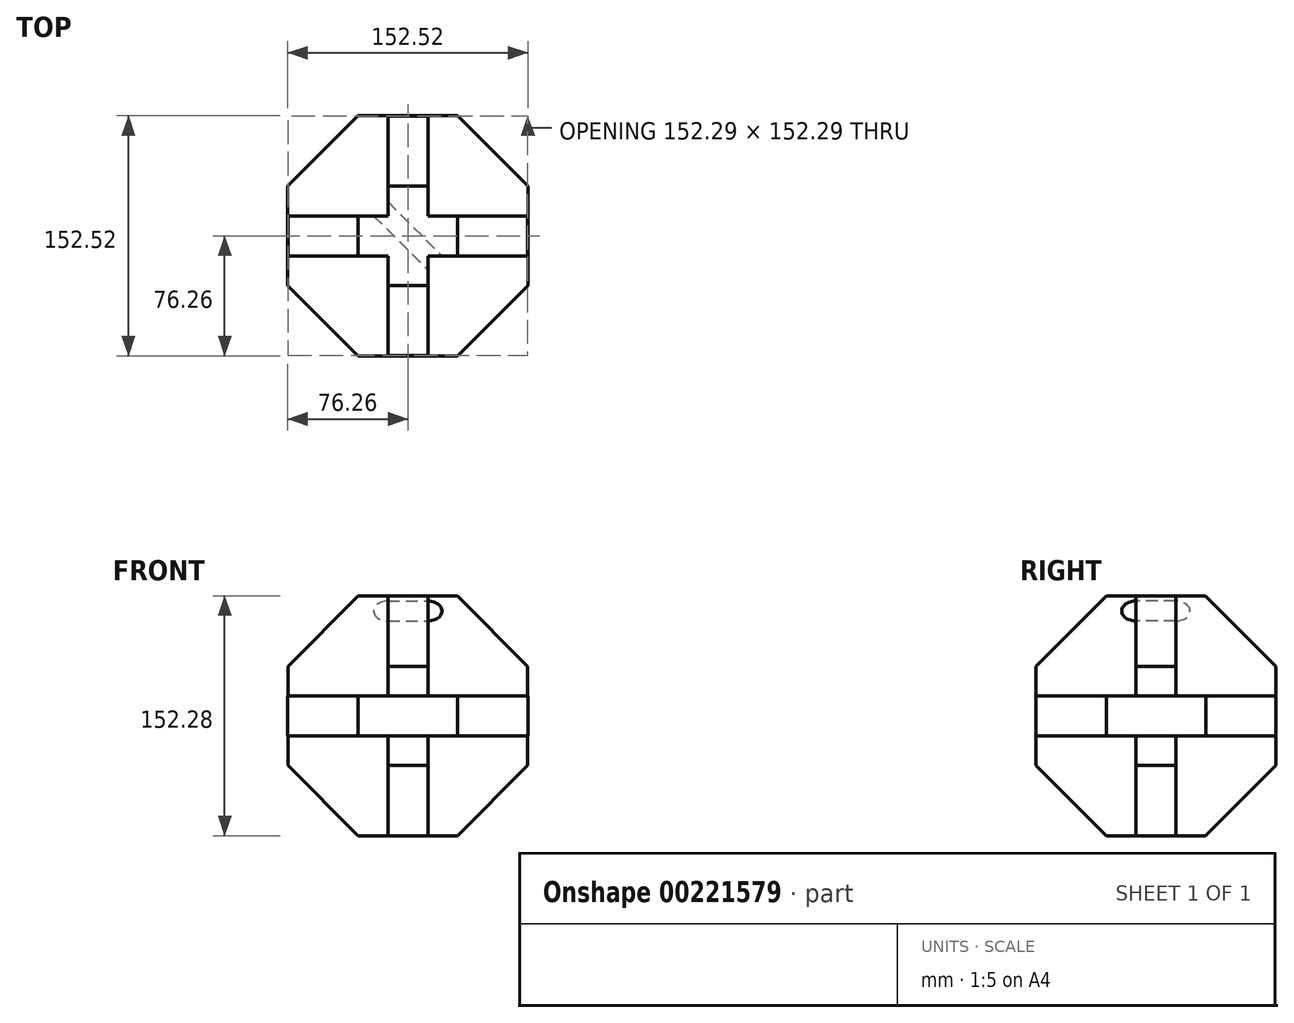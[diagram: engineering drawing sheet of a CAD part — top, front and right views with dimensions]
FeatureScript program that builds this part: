
annotation { "Feature Type Name" : "Feature", "Feature Type Description" : "" }
export const myFeature = defineFeature(function(context is Context, id is Id, definition is map)
    precondition{}
    {
        {
            var Q0;
            Q0=qCreatedBy(makeId("Front.planeOp"),FACE);
            var sketch = newSketch(context, id + "F0", { "sketchPlane" : qUnion([Q0])});
            skCircle(sketch, "E0.cCircle", {"center": v(0, 0) * mm, "radius": 76.14 * mm, "construction": true});
            skLineSegment(sketch, "E0.0", {"start": v(-31.54, 76.14) * mm, "end": v(31.54, 76.14) * mm});
            skLineSegment(sketch, "E0.1", {"start": v(31.54, 76.14) * mm, "end": v(76.14, 31.54) * mm});
            skLineSegment(sketch, "E0.2", {"start": v(76.14, 31.54) * mm, "end": v(76.14, -31.54) * mm});
            skLineSegment(sketch, "E0.3", {"start": v(76.14, -31.54) * mm, "end": v(31.54, -76.14) * mm});
            skLineSegment(sketch, "E0.4", {"start": v(31.54, -76.14) * mm, "end": v(-31.54, -76.14) * mm});
            skLineSegment(sketch, "E0.5", {"start": v(-31.54, -76.14) * mm, "end": v(-76.14, -31.54) * mm});
            skLineSegment(sketch, "E0.6", {"start": v(-76.14, -31.54) * mm, "end": v(-76.14, 31.54) * mm});
            skLineSegment(sketch, "E0.7", {"start": v(-76.14, 31.54) * mm, "end": v(-31.54, 76.14) * mm});
            skPoint(sketch, "E0.0.midPoint", {"position": v(0, 76.14) * mm});
            skSolve(sketch);
        }
        {
            var Q0;
            Q0=makeQuery(id+"F0.imprint","IMPRINT",FACE,{"disambiguationData":[TD([[makeQuery(id+"F0.imprint","IMPRINT",EDGE,{"derivedFrom":sQuery(id+"F0.wireOp",EDGE,"E0.0")}),-1.0]])]});
            extrude(context, id + "F1", {"entities" : qUnion([Q0]), "endBound" : BoundingType.SYMMETRIC, "depth" : 25.4 * mm});
        }
        {
            var Q0;
            Q0=qCreatedBy(makeId("Top.planeOp"),FACE);
            var sketch = newSketch(context, id + "F2", { "sketchPlane" : qUnion([Q0])});
            skCircle(sketch, "E1.cCircle", {"center": v(0, 0) * mm, "radius": 76.26 * mm, "construction": true});
            skLineSegment(sketch, "E1.0", {"start": v(31.59, -76.26) * mm, "end": v(-31.59, -76.26) * mm});
            skLineSegment(sketch, "E1.1", {"start": v(-31.59, -76.26) * mm, "end": v(-76.26, -31.59) * mm});
            skLineSegment(sketch, "E1.2", {"start": v(-76.26, -31.59) * mm, "end": v(-76.26, 31.59) * mm});
            skLineSegment(sketch, "E1.3", {"start": v(-76.26, 31.59) * mm, "end": v(-31.59, 76.26) * mm});
            skLineSegment(sketch, "E1.4", {"start": v(-31.59, 76.26) * mm, "end": v(31.59, 76.26) * mm});
            skLineSegment(sketch, "E1.5", {"start": v(31.59, 76.26) * mm, "end": v(76.26, 31.59) * mm});
            skLineSegment(sketch, "E1.6", {"start": v(76.26, 31.59) * mm, "end": v(76.26, -31.59) * mm});
            skLineSegment(sketch, "E1.7", {"start": v(76.26, -31.59) * mm, "end": v(31.59, -76.26) * mm});
            skPoint(sketch, "E1.0.midPoint", {"position": v(0, -76.26) * mm});
            skSolve(sketch);
        }
        {
            var Q0;
            Q0=makeQuery(id+"F2.imprint","IMPRINT",FACE,{"disambiguationData":[TD([[makeQuery(id+"F2.imprint","IMPRINT",EDGE,{"derivedFrom":sQuery(id+"F2.wireOp",EDGE,"E1.0")}),-1.0]])]});
            extrude(context, id + "F3", {"entities" : qUnion([Q0]), "operationType" : NewBodyOperationType.ADD, "endBound" : BoundingType.SYMMETRIC, "depth" : 25.4 * mm});
        }
        {
            var Q0;
            Q0=qCreatedBy(makeId("Right.planeOp"),FACE);
            var sketch = newSketch(context, id + "F4", { "sketchPlane" : qUnion([Q0])});
            skCircle(sketch, "E2.cCircle", {"center": v(0, 0) * mm, "radius": 76.14 * mm, "construction": true});
            skLineSegment(sketch, "E2.0", {"start": v(-31.54, 76.14) * mm, "end": v(31.54, 76.14) * mm});
            skLineSegment(sketch, "E2.1", {"start": v(31.54, 76.14) * mm, "end": v(76.14, 31.54) * mm});
            skLineSegment(sketch, "E2.2", {"start": v(76.14, 31.54) * mm, "end": v(76.14, -31.54) * mm});
            skLineSegment(sketch, "E2.3", {"start": v(76.14, -31.54) * mm, "end": v(31.54, -76.14) * mm});
            skLineSegment(sketch, "E2.4", {"start": v(31.54, -76.14) * mm, "end": v(-31.54, -76.14) * mm});
            skLineSegment(sketch, "E2.5", {"start": v(-31.54, -76.14) * mm, "end": v(-76.14, -31.54) * mm});
            skLineSegment(sketch, "E2.6", {"start": v(-76.14, -31.54) * mm, "end": v(-76.14, 31.54) * mm});
            skLineSegment(sketch, "E2.7", {"start": v(-76.14, 31.54) * mm, "end": v(-31.54, 76.14) * mm});
            skPoint(sketch, "E2.0.midPoint", {"position": v(0, 76.14) * mm});
            skSolve(sketch);
        }
        {
            var Q0;
            Q0=makeQuery(id+"F4.imprint","IMPRINT",FACE,{"disambiguationData":[TD([[makeQuery(id+"F4.imprint","IMPRINT",EDGE,{"derivedFrom":sQuery(id+"F4.wireOp",EDGE,"E2.0")}),-1.0]])]});
            extrude(context, id + "F5", {"entities" : qUnion([Q0]), "operationType" : NewBodyOperationType.ADD, "endBound" : BoundingType.SYMMETRIC, "depth" : 25.4 * mm});
        }
        {
            var Q0;
            {var subQ0=sQuery(id+"F0.wireOp",EDGE,"E0.2");var subQ1=sQuery(id+"F0.wireOp",EDGE,"E0.6");var subQ2=sQuery(id+"F0.wireOp",EDGE,"E0.1");var subQ3=sQuery(id+"F0.wireOp",EDGE,"E0.0");var subQ4=sQuery(id+"F0.wireOp",EDGE,"E0.7");Q0=makeQuery(id+"F5.boolean.opBoolean","INTERSECT",VERTEX,{"derivedFrom":[makeQuery(id+"F3.boolean.opBoolean","SPLIT",FACE,{"disambiguationData":[TD([makeQuery(id+"F1.opExtrude","SWEPT_FACE",FACE,{"disambiguationData":[OSD([subQ3])]})])],"derivedFrom":makeQuery(id+"F1.opExtrude","CAP_FACE",FACE,{"disambiguationData":[OSD([subQ3,subQ2,subQ0,sQuery(id+"F0.wireOp",EDGE,"E0.3"),sQuery(id+"F0.wireOp",EDGE,"E0.4"),sQuery(id+"F0.wireOp",EDGE,"E0.5"),subQ1,subQ4])],"isStart":false})}),makeQuery(id+"F5.opExtrude","CAP_FACE",FACE,{"disambiguationData":[OSD([sQuery(id+"F4.wireOp",EDGE,"E2.0"),sQuery(id+"F4.wireOp",EDGE,"E2.1"),sQuery(id+"F4.wireOp",EDGE,"E2.2"),sQuery(id+"F4.wireOp",EDGE,"E2.3"),sQuery(id+"F4.wireOp",EDGE,"E2.4"),sQuery(id+"F4.wireOp",EDGE,"E2.5"),sQuery(id+"F4.wireOp",EDGE,"E2.6"),sQuery(id+"F4.wireOp",EDGE,"E2.7")])],"isStart":true})]});}
            var Q1;
            {var subQ0=sQuery(id+"F0.wireOp",EDGE,"E0.2");var subQ1=sQuery(id+"F0.wireOp",EDGE,"E0.6");var subQ2=sQuery(id+"F0.wireOp",EDGE,"E0.1");var subQ3=sQuery(id+"F0.wireOp",EDGE,"E0.0");var subQ4=sQuery(id+"F0.wireOp",EDGE,"E0.7");Q1=makeQuery(id+"F5.boolean.opBoolean","INTERSECT",VERTEX,{"derivedFrom":[makeQuery(id+"F3.boolean.opBoolean","SPLIT",FACE,{"disambiguationData":[TD([makeQuery(id+"F1.opExtrude","SWEPT_FACE",FACE,{"disambiguationData":[OSD([subQ3])]})])],"derivedFrom":makeQuery(id+"F1.opExtrude","CAP_FACE",FACE,{"disambiguationData":[OSD([subQ3,subQ2,subQ0,sQuery(id+"F0.wireOp",EDGE,"E0.3"),sQuery(id+"F0.wireOp",EDGE,"E0.4"),sQuery(id+"F0.wireOp",EDGE,"E0.5"),subQ1,subQ4])],"isStart":true})}),makeQuery(id+"F5.opExtrude","CAP_FACE",FACE,{"disambiguationData":[OSD([sQuery(id+"F4.wireOp",EDGE,"E2.0"),sQuery(id+"F4.wireOp",EDGE,"E2.1"),sQuery(id+"F4.wireOp",EDGE,"E2.2"),sQuery(id+"F4.wireOp",EDGE,"E2.3"),sQuery(id+"F4.wireOp",EDGE,"E2.4"),sQuery(id+"F4.wireOp",EDGE,"E2.5"),sQuery(id+"F4.wireOp",EDGE,"E2.6"),sQuery(id+"F4.wireOp",EDGE,"E2.7")])],"isStart":false})]});}
            var Q2;
            {var subQ0=sQuery(id+"F0.wireOp",EDGE,"E0.5");var subQ1=sQuery(id+"F0.wireOp",EDGE,"E0.4");var subQ2=sQuery(id+"F0.wireOp",EDGE,"E0.3");var subQ3=sQuery(id+"F0.wireOp",EDGE,"E0.2");var subQ4=sQuery(id+"F0.wireOp",EDGE,"E0.6");Q2=makeQuery(id+"F5.boolean.opBoolean","INTERSECT",VERTEX,{"derivedFrom":[makeQuery(id+"F3.boolean.opBoolean","SPLIT",FACE,{"disambiguationData":[TD([makeQuery(id+"F1.opExtrude","SWEPT_FACE",FACE,{"disambiguationData":[OSD([subQ2])]})])],"derivedFrom":makeQuery(id+"F1.opExtrude","CAP_FACE",FACE,{"disambiguationData":[OSD([sQuery(id+"F0.wireOp",EDGE,"E0.0"),sQuery(id+"F0.wireOp",EDGE,"E0.1"),subQ3,subQ2,subQ1,subQ0,subQ4,sQuery(id+"F0.wireOp",EDGE,"E0.7")])],"isStart":true})}),makeQuery(id+"F5.opExtrude","CAP_FACE",FACE,{"disambiguationData":[OSD([sQuery(id+"F4.wireOp",EDGE,"E2.0"),sQuery(id+"F4.wireOp",EDGE,"E2.1"),sQuery(id+"F4.wireOp",EDGE,"E2.2"),sQuery(id+"F4.wireOp",EDGE,"E2.3"),sQuery(id+"F4.wireOp",EDGE,"E2.4"),sQuery(id+"F4.wireOp",EDGE,"E2.5"),sQuery(id+"F4.wireOp",EDGE,"E2.6"),sQuery(id+"F4.wireOp",EDGE,"E2.7")])],"isStart":false})]});}
            cPlane(context, id + "F6", {"entities" : qUnion([Q0, Q1, Q2]), "cplaneType" : CPlaneType.THREE_POINT, "offset" : 25.4 * mm, "width" : 152.4 * mm, "height" : 152.4 * mm});
        }
        {
            var Q0;
            Q0=qCreatedBy(id+"F6.planeOp",FACE);
            var sketch = newSketch(context, id + "F7", { "sketchPlane" : qUnion([Q0])});
            skCircle(sketch, "E3", {"center": v(0, 66.61) * mm, "radius": 6.35 * mm});
            skSolve(sketch);
        }
        {
            var Q0;
            Q0 = qSketchRegion(id + "F7", true);
            var Q1;
            Q1=sQuery(id+"F7.wireOp",EDGE,"E3");
            extrude(context, id + "F8", {"entities" : qUnion([Q0]), "operationType" : NewBodyOperationType.REMOVE, "surfaceEntities" : qUnion([Q1]), "endBound" : BoundingType.SYMMETRIC, "oppositeDirection" : true, "depth" : 127 * mm});
        }
    });
